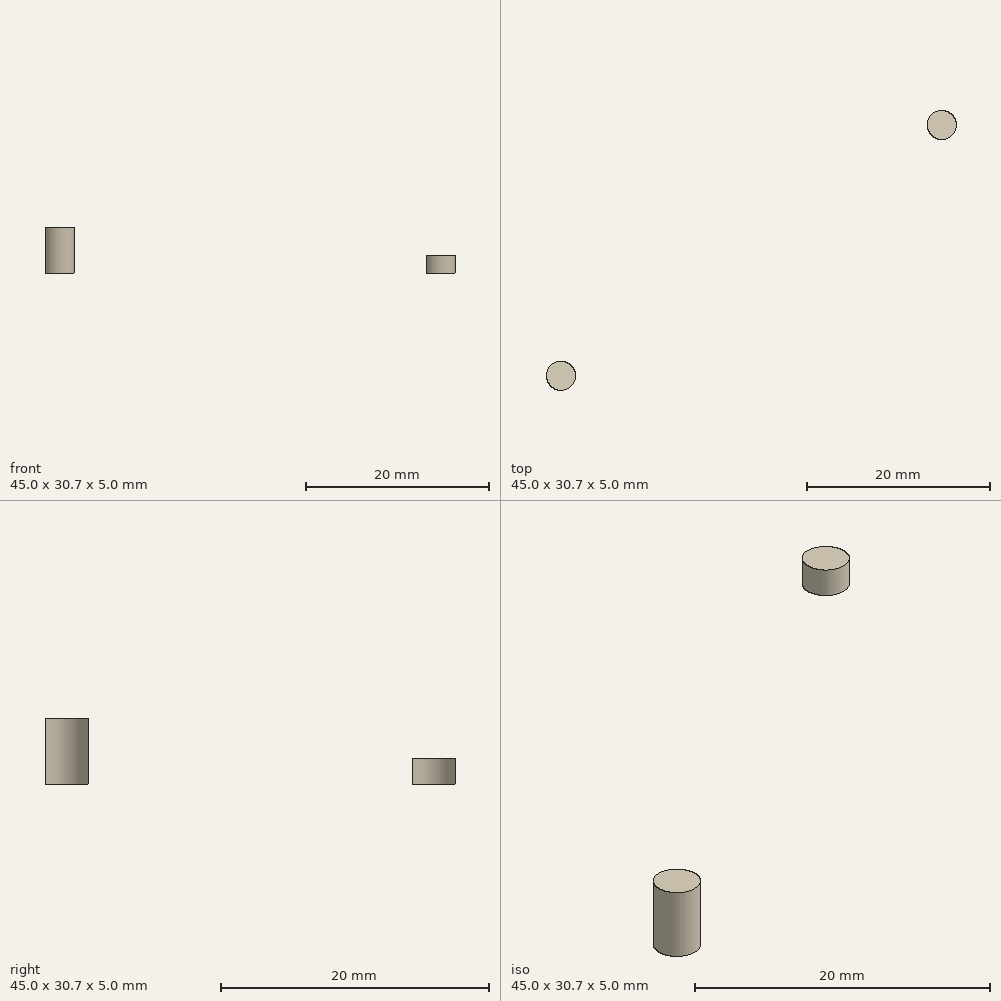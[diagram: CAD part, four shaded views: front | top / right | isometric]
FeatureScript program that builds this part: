
annotation { "Feature Type Name" : "Feature", "Feature Type Description" : "" }
export const myFeature = defineFeature(function(context is Context, id is Id, definition is map)
    precondition{}
    {
        {
            var Q0;
            Q0=qCreatedBy(makeId("Top.planeOp"),FACE);
            var sketch = newSketch(context, id + "F0", { "sketchPlane" : qUnion([Q0])});
            skCircle(sketch, "E0", {"center": v(0, 0) * mm, "radius": 50 * mm});
            skSolve(sketch);
        }
        {
            var Q0;
            Q0=makeQuery(id+"F0.imprint","IMPRINT",FACE,{"disambiguationData":[TD([[makeQuery(id+"F0.imprint","IMPRINT",EDGE,{"derivedFrom":sQuery(id+"F0.wireOp",EDGE,"E0")}),1.0]])]});
            extrude(context, id + "F1", {"entities" : qUnion([Q0]), "depth" : 5 * mm, "offsetDistance" : 25 * mm});
        }
        {
            var Q0;
            Q0=makeQuery(id+"F1.opExtrude","CAP_FACE",FACE,{"disambiguationData":[OSD([sQuery(id+"F0.wireOp",EDGE,"E0")])],"isStart":false});
            var sketch = newSketch(context, id + "F2", { "sketchPlane" : qUnion([Q0])});
            skCircle(sketch, "E1", {"center": v(0, 0) * mm, "radius": 8 * mm});
            skSolve(sketch);
        }
        {
            var Q0;
            Q0=makeQuery(id+"F2.imprint","IMPRINT",FACE,{"disambiguationData":[TD([[makeQuery(id+"F2.imprint","IMPRINT",EDGE,{"derivedFrom":sQuery(id+"F2.wireOp",EDGE,"E1")}),1.0]])]});
            extrude(context, id + "F3", {"entities" : qUnion([Q0]), "operationType" : NewBodyOperationType.REMOVE, "oppositeDirection" : true, "depth" : 5 * mm, "offsetDistance" : 25 * mm});
        }
        {
            var Q0;
            Q0=makeQuery(id+"F1.opExtrude","CAP_FACE",FACE,{"disambiguationData":[OSD([sQuery(id+"F0.wireOp",EDGE,"E0")])],"isStart":true});
            var sketch = newSketch(context, id + "F4", { "sketchPlane" : qUnion([Q0])});
            skCircle(sketch, "E2", {"center": v(0, 0) * mm, "radius": 6.55 * mm});
            skSolve(sketch);
        }
        {
            var Q0;
            Q0=makeQuery(id+"F4.imprint","IMPRINT",FACE,{"disambiguationData":[TD([[makeQuery(id+"F4.imprint","IMPRINT",EDGE,{"derivedFrom":sQuery(id+"F4.wireOp",EDGE,"E2")}),1.0]])]});
            var Q1;
            Q1=sQuery(id+"F4.wireOp",EDGE,"E2");
            extrude(context, id + "F5", {"entities" : qUnion([Q0]), "operationType" : NewBodyOperationType.REMOVE, "surfaceEntities" : qUnion([Q1]), "oppositeDirection" : true, "depth" : 25 * mm, "offsetDistance" : 25 * mm});
        }
        {
            var Q0;
            Q0=makeQuery(id+"F1.opExtrude","CAP_FACE",FACE,{"disambiguationData":[OSD([sQuery(id+"F0.wireOp",EDGE,"E0")])],"isStart":false});
            var sketch = newSketch(context, id + "F6", { "sketchPlane" : qUnion([Q0])});
            skCircle(sketch, "E3", {"center": v(0, 0) * mm, "radius": 40 * mm, "construction": true});
            skCircle(sketch, "E4", {"center": v(-40, 0) * mm, "radius": 3 * mm});
            skCircle(sketch, "E5.1.0", {"center": v(0, -40) * mm, "radius": 3 * mm});
            skCircle(sketch, "E5.2.0", {"center": v(40, 0) * mm, "radius": 3 * mm});
            skCircle(sketch, "E5.3.0", {"center": v(0, 40) * mm, "radius": 3 * mm});
            skSolve(sketch);
        }
        {
            var Q0;
            Q0=makeQuery(id+"F6.imprint","IMPRINT",FACE,{"disambiguationData":[TD([[makeQuery(id+"F6.imprint","IMPRINT",EDGE,{"derivedFrom":sQuery(id+"F6.wireOp",EDGE,"E5.3.0")}),1.0]])]});
            var Q1;
            Q1=makeQuery(id+"F6.imprint","IMPRINT",FACE,{"disambiguationData":[TD([[makeQuery(id+"F6.imprint","IMPRINT",EDGE,{"derivedFrom":sQuery(id+"F6.wireOp",EDGE,"E4")}),1.0]])]});
            var Q2;
            Q2=makeQuery(id+"F6.imprint","IMPRINT",FACE,{"disambiguationData":[TD([[makeQuery(id+"F6.imprint","IMPRINT",EDGE,{"derivedFrom":sQuery(id+"F6.wireOp",EDGE,"E5.1.0")}),1.0]])]});
            var Q3;
            Q3=makeQuery(id+"F6.imprint","IMPRINT",FACE,{"disambiguationData":[TD([[makeQuery(id+"F6.imprint","IMPRINT",EDGE,{"derivedFrom":sQuery(id+"F6.wireOp",EDGE,"E5.2.0")}),1.0]])]});
            extrude(context, id + "F7", {"entities" : qUnion([Q0, Q1, Q2, Q3]), "operationType" : NewBodyOperationType.REMOVE, "oppositeDirection" : true, "depth" : 25 * mm, "offsetDistance" : 25 * mm});
        }
        {
            var Q0;
            Q0=makeQuery(id+"F1.opExtrude","CAP_FACE",FACE,{"disambiguationData":[OSD([sQuery(id+"F0.wireOp",EDGE,"E0")])],"isStart":false});
            var sketch = newSketch(context, id + "F8", { "sketchPlane" : qUnion([Q0])});
            skCircle(sketch, "E6", {"center": v(0, 0) * mm, "radius": 35.31 * mm, "construction": true});
            skLineSegment(sketch, "E7", {"start": v(24.97, 24.97) * mm, "end": v(-47.65, -47.65) * mm, "construction": true});
            skCircle(sketch, "E8", {"center": v(-21.14, -28.28) * mm, "radius": 1.6 * mm});
            skCircle(sketch, "E9.MirrorC", {"center": v(-28.28, -21.14) * mm, "radius": 1.6 * mm});
            skCircle(sketch, "E10", {"center": v(0, 0) * mm, "radius": 14.93 * mm, "construction": true});
            skCircle(sketch, "E11", {"center": v(6.36, 13.5) * mm, "radius": 1.6 * mm});
            skCircle(sketch, "E12.MirrorC", {"center": v(13.5, 6.36) * mm, "radius": 1.6 * mm});
            skSolve(sketch);
        }
        {
            var Q0;
            Q0=makeQuery(id+"F8.imprint","IMPRINT",FACE,{"disambiguationData":[TD([[makeQuery(id+"F8.imprint","IMPRINT",EDGE,{"derivedFrom":sQuery(id+"F8.wireOp",EDGE,"E8")}),1.0]])]});
            var Q1;
            Q1=makeQuery(id+"F8.imprint","IMPRINT",FACE,{"disambiguationData":[TD([[makeQuery(id+"F8.imprint","IMPRINT",EDGE,{"derivedFrom":sQuery(id+"F8.wireOp",EDGE,"E9.MirrorC")}),-1.0]])]});
            var Q2;
            Q2=makeQuery(id+"F8.imprint","IMPRINT",FACE,{"disambiguationData":[TD([[makeQuery(id+"F8.imprint","IMPRINT",EDGE,{"derivedFrom":sQuery(id+"F8.wireOp",EDGE,"E11")}),1.0]])]});
            var Q3;
            Q3=makeQuery(id+"F8.imprint","IMPRINT",FACE,{"disambiguationData":[TD([[makeQuery(id+"F8.imprint","IMPRINT",EDGE,{"derivedFrom":sQuery(id+"F8.wireOp",EDGE,"E12.MirrorC")}),-1.0]])]});
            var Q4;
            Q4=sQuery(id+"F8.wireOp",EDGE,"E9.MirrorC");
            var Q5;
            Q5=sQuery(id+"F8.wireOp",EDGE,"E8");
            extrude(context, id + "F9", {"entities" : qUnion([Q0, Q1, Q2, Q3]), "operationType" : NewBodyOperationType.REMOVE, "surfaceEntities" : qUnion([Q4, Q5]), "oppositeDirection" : true, "depth" : 25 * mm, "offsetDistance" : 25 * mm});
        }
        {
            var Q0;
            Q0=makeQuery(id+"F1.opExtrude","CAP_FACE",FACE,{"disambiguationData":[OSD([sQuery(id+"F0.wireOp",EDGE,"E0")])],"isStart":false});
            var sketch = newSketch(context, id + "F10", { "sketchPlane" : qUnion([Q0])});
            skCircle(sketch, "E13", {"center": v(6.36, 13.5) * mm, "radius": 2.9 * mm});
            skCircle(sketch, "E14", {"center": v(13.5, 6.36) * mm, "radius": 2.9 * mm});
            skCircle(sketch, "E15", {"center": v(-28.28, -21.14) * mm, "radius": 2.9 * mm});
            skCircle(sketch, "E16", {"center": v(-21.14, -28.28) * mm, "radius": 2.9 * mm});
            skSolve(sketch);
        }
        {
            var Q0;
            Q0=makeQuery(id+"F10.imprint","IMPRINT",FACE,{"disambiguationData":[TD([[makeQuery(id+"F10.imprint","IMPRINT",EDGE,{"derivedFrom":sQuery(id+"F10.wireOp",EDGE,"E13")}),1.0]])]});
            var Q1;
            Q1=makeQuery(id+"F10.imprint","IMPRINT",FACE,{"disambiguationData":[TD([[makeQuery(id+"F10.imprint","IMPRINT",EDGE,{"derivedFrom":sQuery(id+"F10.wireOp",EDGE,"E14")}),1.0]])]});
            var Q2;
            Q2=makeQuery(id+"F10.imprint","IMPRINT",FACE,{"disambiguationData":[TD([[makeQuery(id+"F10.imprint","IMPRINT",EDGE,{"derivedFrom":sQuery(id+"F10.wireOp",EDGE,"E15")}),1.0]])]});
            var Q3;
            Q3=makeQuery(id+"F10.imprint","IMPRINT",FACE,{"disambiguationData":[TD([[makeQuery(id+"F10.imprint","IMPRINT",EDGE,{"derivedFrom":sQuery(id+"F10.wireOp",EDGE,"E16")}),1.0]])]});
            var Q4;
            Q4=sQuery(id+"F10.wireOp",EDGE,"E14");
            var Q5;
            Q5=sQuery(id+"F10.wireOp",EDGE,"E13");
            extrude(context, id + "F11", {"entities" : qUnion([Q0, Q1, Q2, Q3]), "operationType" : NewBodyOperationType.REMOVE, "surfaceEntities" : qUnion([Q4, Q5]), "oppositeDirection" : true, "depth" : 3 * mm, "offsetDistance" : 25 * mm});
        }
    });
